# Revit family: Олимп_Скамейка
name_source: partatom
category: Мебель
revit_build: Autodesk Revit 2017 (Build: 20160225_1515(x64)
units: mm (PartAtom-declared; Revit-internal decimal feet)

## family parameters
Всегда вертикально = Да
Заголовок OmniClass = General Furniture and Specialties
На основе рабочей плоскости = Нет
Номер OmniClass = 23.40.20.00
Общий = Нет
При загрузке вырезать с полостями = Нет
Точка расчета площади = Нет

## types (6) — shared parameters
ADSK_Код изделия = 7061
ADSK_Материал доски = <По категории>
ADSK_Материал опоры = <По категории>
ADSK_Материал рекламного щита = <По категории>
ADSK_Материал фурнитуры = <По категории>
ADSK_Размер_Высота = 970 мм
ADSK_Размер_Высота сидения = 440 мм
ADSK_Размер_Ширина = 670 мм
ADSK_Размер_Ширина сидения = 420 мм
URL = https://hobbyka.ru
Изготовитель = ООО "Хоббика"

## per-type parameters (varying)
| type | ADSK_Размер_Длина | Длина доски | Длина доски на спинке | Перемычка | С_Количество_опор_Видимость | Стоимость |
| Скамейка «Олимп» 1,2м | 1200 мм | 1186 мм | 1186 мм | Да | Нет | 7527 $ |
| Скамейка «Олимп» 1,5м | 1500 мм | 1486 мм | 1486 мм | Да | Нет | 8652 $ |
| Скамейка «Олимп» 1,8м | 1800 мм | 1786 мм | 1786 мм | Да | Нет | 9776 $ |
| Скамейка «Олимп» 2,0м | 2000 мм | 1986 мм | 1986 мм | Нет | Да | 14270 $ |
| Скамейка «Олимп» 3,0м | 3000 мм | 2986 мм | 2986 мм | Нет | Да | 15320 $ |
| Скамейка «Олимп» Кресло | 600 мм | 586 мм | 586 мм | Да | Нет | 6405 $ |

note: column(s) folded — value = type name in every type: ADSK_Наименование
